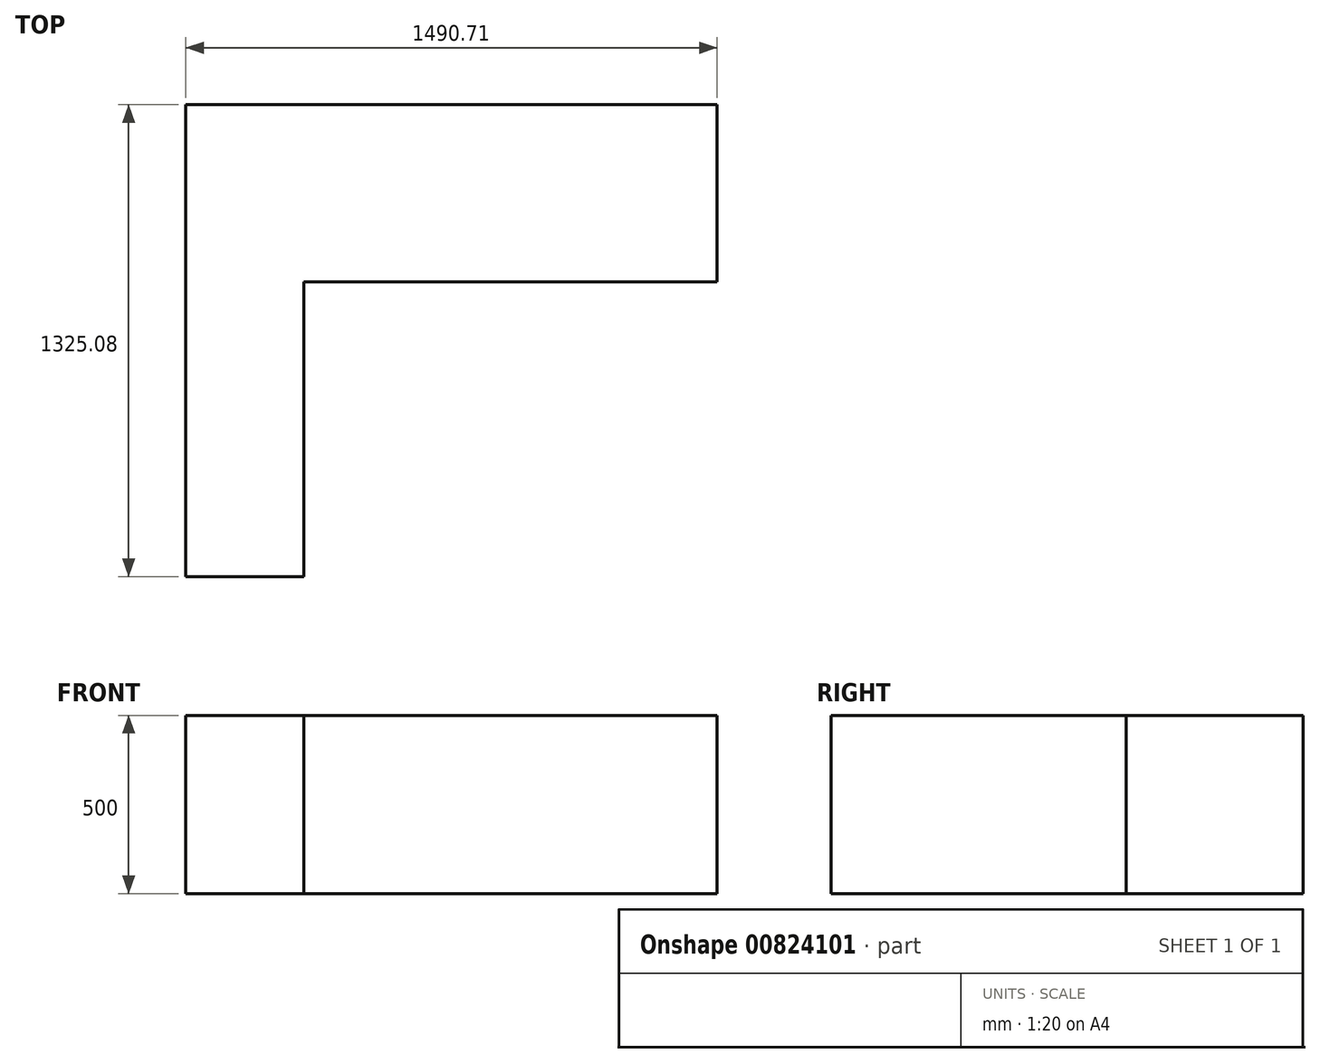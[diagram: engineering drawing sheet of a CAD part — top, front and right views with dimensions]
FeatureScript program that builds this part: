
annotation { "Feature Type Name" : "Feature", "Feature Type Description" : "" }
export const myFeature = defineFeature(function(context is Context, id is Id, definition is map)
    precondition{}
    {
        {
            var Q0;
            Q0=qCreatedBy(makeId("Top.planeOp"),FACE);
            var sketch = newSketch(context, id + "F0", { "sketchPlane" : qUnion([Q0])});
            skLineSegment(sketch, "E0.bottom", {"start": v(-2496.64, 1669.93) * mm, "end": v(2496.64, 1669.93) * mm});
            skLineSegment(sketch, "E0.left", {"start": v(-2496.64, 1669.93) * mm, "end": v(-2496.64, -1658.93) * mm});
            skLineSegment(sketch, "E0.right", {"start": v(2496.64, 1669.93) * mm, "end": v(2496.64, -1658.93) * mm});
            skPoint(sketch, "E0.middle", {"position": v(0, 5.5) * mm});
            skLineSegment(sketch, "E1", {"start": v(-2496.64, -1658.93) * mm, "end": v(2496.64, -1658.93) * mm});
            skLineSegment(sketch, "E2", {"start": v(-2496.64, 1669.93) * mm, "end": v(-1005.93, 1669.93) * mm});
            skLineSegment(sketch, "E3", {"start": v(-1005.93, 1669.93) * mm, "end": v(-1005.93, 1173.02) * mm});
            skLineSegment(sketch, "E4", {"start": v(-1005.93, 1173.02) * mm, "end": v(-2165.37, 1173.02) * mm});
            skLineSegment(sketch, "E5", {"start": v(-2165.37, 1173.02) * mm, "end": v(-2165.37, 344.85) * mm});
            skLineSegment(sketch, "E6", {"start": v(-2165.37, 344.85) * mm, "end": v(-2496.64, 344.85) * mm});
            skLineSegment(sketch, "E7", {"start": v(-2496.64, 344.85) * mm, "end": v(-2496.64, 1669.93) * mm});
            skLineSegment(sketch, "E8.bottom", {"start": v(2496.64, 1669.93) * mm, "end": v(1596.64, 1669.93) * mm});
            skLineSegment(sketch, "E8.top", {"start": v(2496.64, -230.07) * mm, "end": v(1596.64, -230.07) * mm});
            skLineSegment(sketch, "E8.left", {"start": v(2496.64, 1669.93) * mm, "end": v(2496.64, -230.07) * mm});
            skLineSegment(sketch, "E8.right", {"start": v(1596.64, 1669.93) * mm, "end": v(1596.64, -230.07) * mm});
            skLineSegment(sketch, "E9.bottom", {"start": v(1596.64, 1669.93) * mm, "end": v(2496.64, 1669.93) * mm});
            skLineSegment(sketch, "E9.top", {"start": v(1596.64, 1413.15) * mm, "end": v(2496.64, 1413.15) * mm});
            skLineSegment(sketch, "E9.left", {"start": v(1596.64, 1669.93) * mm, "end": v(1596.64, 1413.15) * mm});
            skLineSegment(sketch, "E9.right", {"start": v(2496.64, 1669.93) * mm, "end": v(2496.64, 1413.15) * mm});
            skLineSegment(sketch, "E10", {"start": v(1596.64, 1139.54) * mm, "end": v(2496.64, 1413.15) * mm});
            skSolve(sketch);
        }
        {
            var Q0;
            Q0=makeQuery(id+"F0.imprint","IMPRINT",FACE,{"disambiguationData":[TD([[makeQuery(id+"F0.imprint","IMPRINT",EDGE,{"derivedFrom":sQuery(id+"F0.wireOp",EDGE,"E8.bottom")}),1.0]])]});
            var Q1;
            {var subQ0=sQuery(id+"F0.wireOp",EDGE,"E3");Q1=makeQuery(id+"F0.imprint","IMPRINT",FACE,{"disambiguationData":[TD([[makeQuery(id+"F0.imprint","IMPRINT",EDGE,{"derivedFrom":subQ0}),-1.0]])]});}
            extrude(context, id + "F1", {"entities" : qUnion([Q0, Q1]), "depth" : 500 * mm, "offsetDistance" : 25 * mm});
        }
    });
